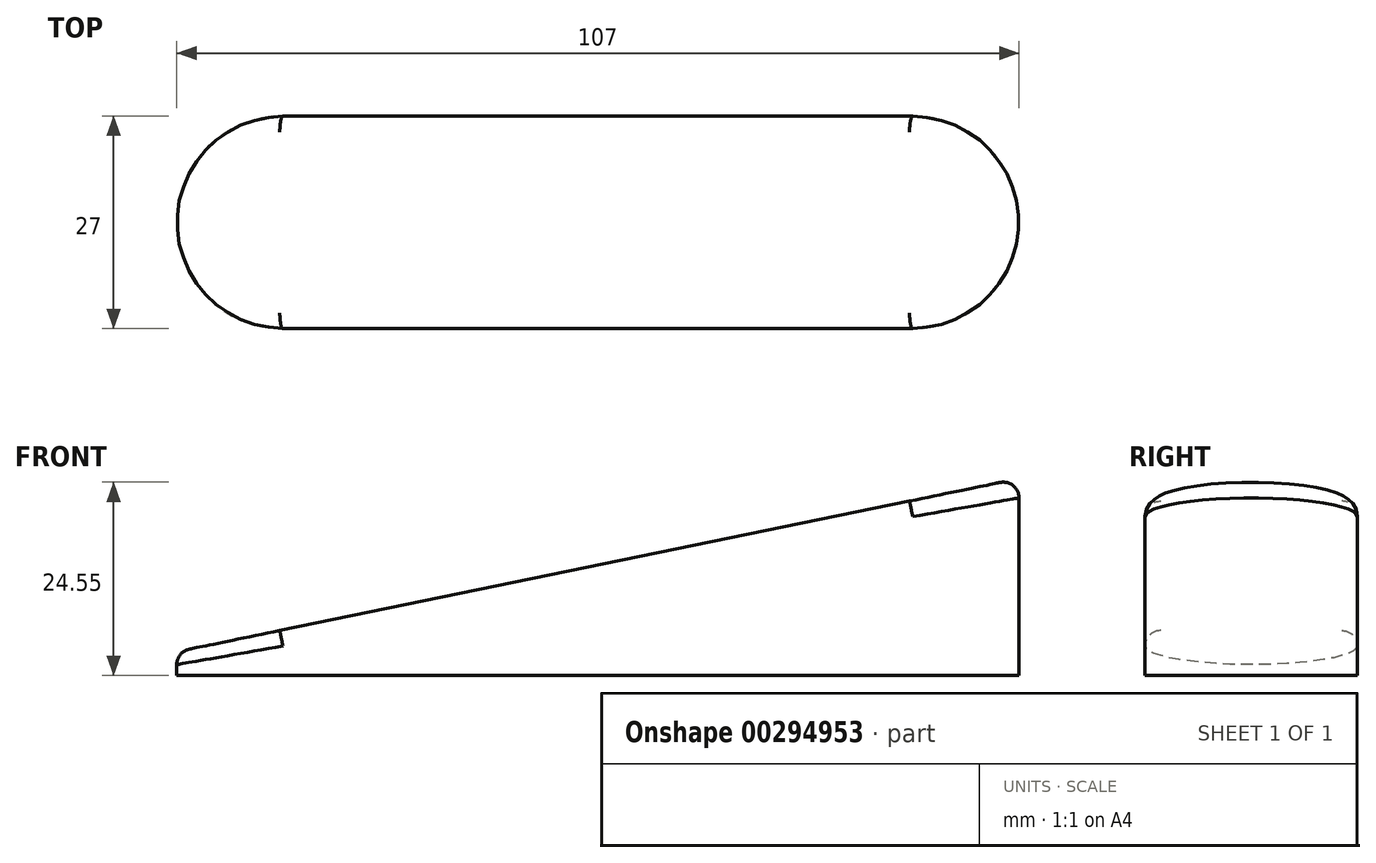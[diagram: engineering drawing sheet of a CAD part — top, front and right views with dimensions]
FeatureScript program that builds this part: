
annotation { "Feature Type Name" : "Feature", "Feature Type Description" : "" }
export const myFeature = defineFeature(function(context is Context, id is Id, definition is map)
    precondition{}
    {
        {
            var Q0;
            Q0=qCreatedBy(makeId("Top.planeOp"),FACE);
            var sketch = newSketch(context, id + "F0", { "sketchPlane" : qUnion([Q0])});
            skLineSegment(sketch, "E0", {"start": v(-40, 0) * mm, "end": v(40, 0) * mm});
            skArc(sketch, "E1.0.startCap", {"start": v(-40, -13.5) * mm, "mid": v(-53.5, 0) * mm, "end": v(-40, 13.5) * mm});
            skArc(sketch, "E1.0.endCap", {"start": v(40, 13.5) * mm, "mid": v(53.5, 0) * mm, "end": v(40, -13.5) * mm});
            skLineSegment(sketch, "E1.0.left", {"start": v(-40, 13.5) * mm, "end": v(40, 13.5) * mm});
            skLineSegment(sketch, "E1.0.right", {"start": v(-40, -13.5) * mm, "end": v(40, -13.5) * mm});
            skSolve(sketch);
        }
        {
            var Q0;
            Q0=qSketchRegion(id+"F0",true);
            extrude(context, id + "F1", {"entities" : qUnion([Q0]), "depth" : 25 * mm});
        }
        {
            var Q0;
            Q0=qCreatedBy(makeId("Front.planeOp"),FACE);
            var sketch = newSketch(context, id + "F2", { "sketchPlane" : qUnion([Q0])});
            skLineSegment(sketch, "E2", {"start": v(-53.5, 3) * mm, "end": v(53.5, 25) * mm});
            skLineSegment(sketch, "E3", {"start": v(53.5, 25) * mm, "end": v(-53.5, 25) * mm});
            skLineSegment(sketch, "E4", {"start": v(-53.5, 25) * mm, "end": v(-53.5, 3) * mm});
            skSolve(sketch);
        }
        {
            var Q0;
            Q0=qSketchRegion(id+"F2",true);
            extrude(context, id + "F3", {"entities" : qUnion([Q0]), "operationType" : NewBodyOperationType.REMOVE, "oppositeDirection" : true, "depth" : 25 * mm, "hasSecondDirection" : true, "secondDirectionOppositeDirection" : false, "secondDirectionDepth" : 25 * mm});
        }
        {
            var Q0;
            Q0=makeQuery(id+"F3.boolean.opBoolean","COPY",FACE,{"derivedFrom":makeQuery(id+"F3.opExtrude","SWEPT_FACE",FACE,{"disambiguationData":[OSD([sQuery(id+"F2.wireOp",EDGE,"E2")])]})});
            fillet(context, id + "F4", {"entities" : qUnion([Q0]), "radius" : 2 * mm, "tangentPropagation" : true, "allowEdgeOverflow" : false});
        }
    });
